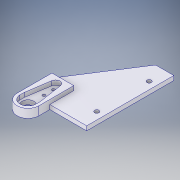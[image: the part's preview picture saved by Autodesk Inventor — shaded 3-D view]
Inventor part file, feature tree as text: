
AUTODESK INVENTOR PART (.ipt)
format: ipt  version: 2017 (Build 210142000, 142)  size: 155,648 bytes
history: native  units: in
note: dims shown in document units (in); Inventor stores cm internally (conversion verified against a paired STEP export)
features: extrude x2, sketch x2, projected_geometry x1
ambient origin geometry x8: Origin, YZ Plane, XZ Plane, XY Plane, X Axis, Y Axis, Z Axis, Center Point
bodies: Solid1 (feature_tree)
feature tree (5):
  extrude  "Extrusion1"  TaperAngle=90.0deg  [1 undecoded]
  extrude  "Extrusion3"  Depth=1.0in
  sketch  "Sketch3"  dims[d6=2.3622in d7=90.0deg]
  sketch  "Sketch6"  dims[d8=0.4929in d9=1.0in d10=0.2953in d11=0.5906in d13=0.9456in d14=0.1181in d15=0.0in d18=0.1969in d19=0.4724in d20=0.4724in d21=0.1181in d22=0.1181in d25=0.315in d26=0.4335in d27=0.2562in d28=0.0787in d29=0.0787in d31=0.4331in d32=0.0591in d33=0.2362in d34=0.1181in d35=0.1181in d36=0.0in]
  projected_geometry  "Projected Loop3"
note: 1 required parameter value undecoded (feature->parameter linkage not recoverable at this tier; creation-order binding heuristic only, values carry confidence <= 0.55)
